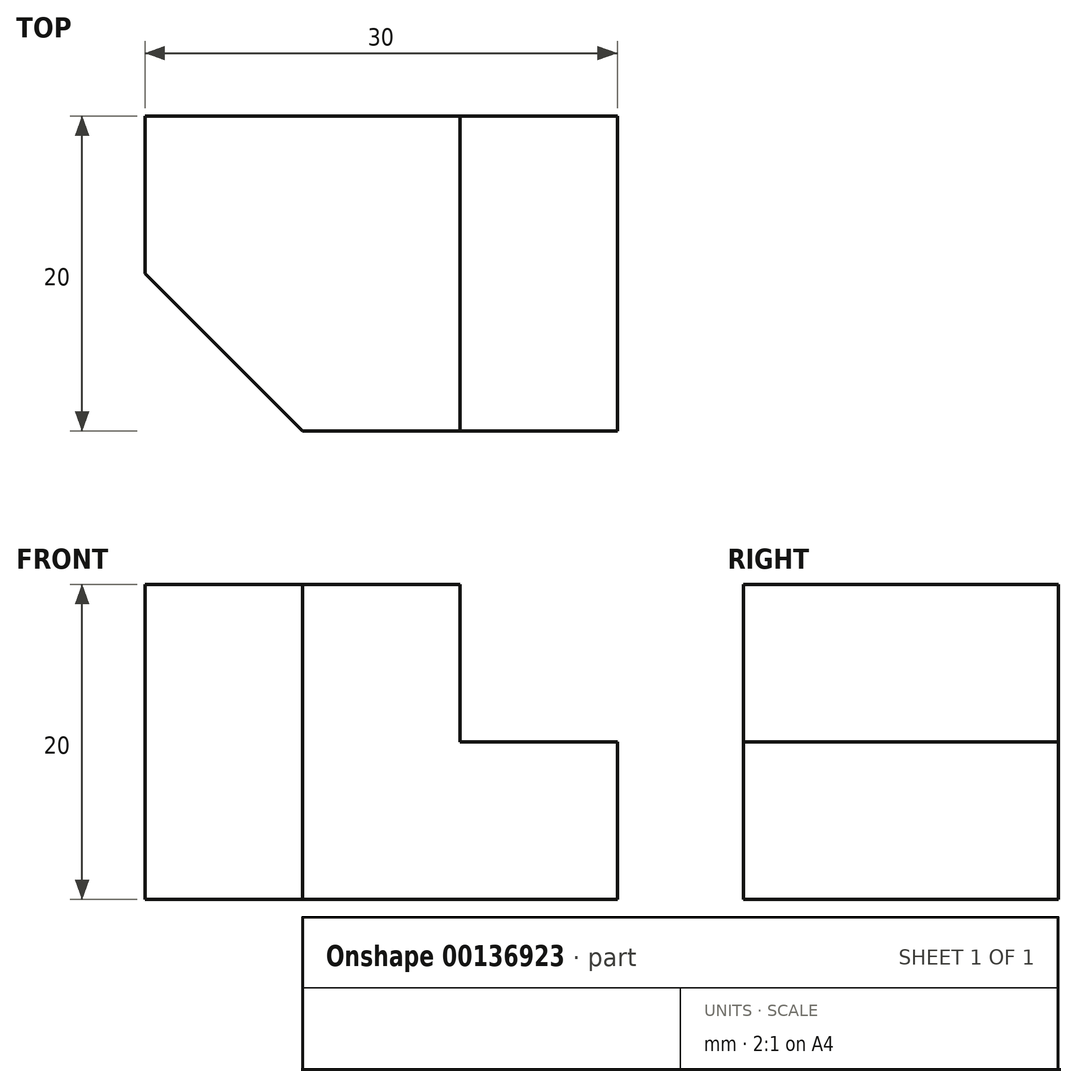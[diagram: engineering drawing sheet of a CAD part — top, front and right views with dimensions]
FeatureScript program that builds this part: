
annotation { "Feature Type Name" : "Feature", "Feature Type Description" : "" }
export const myFeature = defineFeature(function(context is Context, id is Id, definition is map)
    precondition{}
    {
        {
            var Q0;
            Q0=qCreatedBy(makeId("Top.planeOp"),FACE);
            var sketch = newSketch(context, id + "F0", { "sketchPlane" : qUnion([Q0])});
            skLineSegment(sketch, "E0", {"start": v(0, 0) * mm, "end": v(0, 20) * mm});
            skLineSegment(sketch, "E1", {"start": v(0, 20) * mm, "end": v(-30, 20) * mm});
            skLineSegment(sketch, "E2", {"start": v(-30, 20) * mm, "end": v(-30, 10) * mm});
            skLineSegment(sketch, "E3", {"start": v(-30, 10) * mm, "end": v(-20, 0) * mm});
            skLineSegment(sketch, "E4", {"start": v(-20, 0) * mm, "end": v(0, 0) * mm});
            skSolve(sketch);
        }
        {
            var Q0;
            Q0 = qSketchRegion(id + "F0", true);
            extrude(context, id + "F1", {"entities" : qUnion([Q0]), "depth" : 20 * mm});
        }
        {
            var Q0;
            Q0=makeQuery(id+"F1.opExtrude","SWEPT_FACE",FACE,{"disambiguationData":[OSD([sQuery(id+"F0.wireOp",EDGE,"E4")])]});
            var sketch = newSketch(context, id + "F2", { "sketchPlane" : qUnion([Q0])});
            skLineSegment(sketch, "E5.bottom", {"start": v(0, 20) * mm, "end": v(-10, 20) * mm});
            skLineSegment(sketch, "E5.top", {"start": v(0, 10) * mm, "end": v(-10, 10) * mm});
            skLineSegment(sketch, "E5.left", {"start": v(0, 20) * mm, "end": v(0, 10) * mm});
            skLineSegment(sketch, "E5.right", {"start": v(-10, 20) * mm, "end": v(-10, 10) * mm});
            skSolve(sketch);
        }
        {
            var Q0;
            Q0 = qSketchRegion(id + "F2", true);
            extrude(context, id + "F3", {"entities" : qUnion([Q0]), "operationType" : NewBodyOperationType.REMOVE, "endBound" : BoundingType.THROUGH_ALL, "oppositeDirection" : true, "depth" : 25 * mm});
        }
    });
